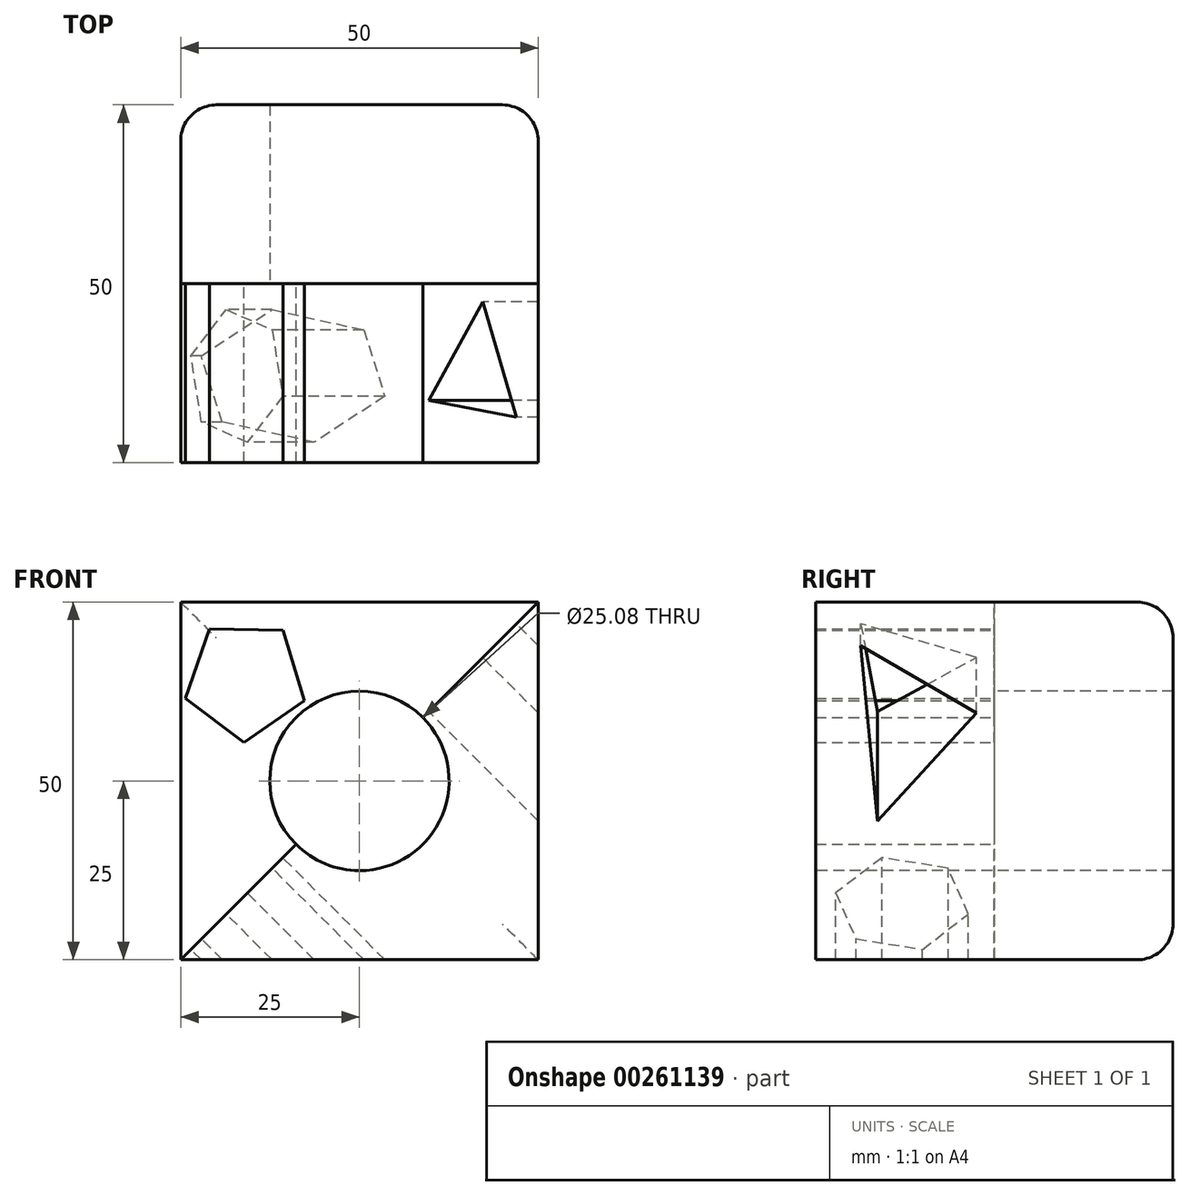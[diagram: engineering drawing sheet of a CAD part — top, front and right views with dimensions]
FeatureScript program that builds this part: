
annotation { "Feature Type Name" : "Feature", "Feature Type Description" : "" }
export const myFeature = defineFeature(function(context is Context, id is Id, definition is map)
    precondition{}
    {
        {
            var Q0;
            Q0=qCreatedBy(makeId("Front.planeOp"),FACE);
            var sketch = newSketch(context, id + "F0", { "sketchPlane" : qUnion([Q0])});
            skLineSegment(sketch, "E0", {"start": v(-25, 25) * mm, "end": v(-25, -25) * mm});
            skLineSegment(sketch, "E1", {"start": v(-25, -25) * mm, "end": v(25, -25) * mm});
            skLineSegment(sketch, "E2", {"start": v(25, -25) * mm, "end": v(25, 25) * mm});
            skLineSegment(sketch, "E3", {"start": v(25, 25) * mm, "end": v(-25, 25) * mm});
            skSolve(sketch);
        }
        {
            var Q0;
            Q0=makeQuery(id+"F0.imprint","IMPRINT",FACE,{"disambiguationData":[TD([[makeQuery(id+"F0.imprint","IMPRINT",EDGE,{"derivedFrom":sQuery(id+"F0.wireOp",EDGE,"E0")}),1.0]])]});
            extrude(context, id + "F1", {"entities" : qUnion([Q0]), "depth" : 25 * mm});
        }
        {
            var Q0;
            Q0=makeQuery(id+"F1.opExtrude","CAP_FACE",FACE,{"disambiguationData":[OSD([sQuery(id+"F0.wireOp",EDGE,"E0"),sQuery(id+"F0.wireOp",EDGE,"E1"),sQuery(id+"F0.wireOp",EDGE,"E2"),sQuery(id+"F0.wireOp",EDGE,"E3")])],"isStart":false});
            var sketch = newSketch(context, id + "F2", { "sketchPlane" : qUnion([Q0])});
            skCircle(sketch, "E4", {"center": v(0, 0) * mm, "radius": 12.54 * mm});
            skSolve(sketch);
        }
        {
            var Q0;
            Q0=makeQuery(id+"F2.imprint","IMPRINT",FACE,{"disambiguationData":[TD([[makeQuery(id+"F2.imprint","IMPRINT",EDGE,{"derivedFrom":sQuery(id+"F2.wireOp",EDGE,"E4")}),1.0]])]});
            extrude(context, id + "F3", {"entities" : qUnion([Q0]), "operationType" : NewBodyOperationType.REMOVE, "oppositeDirection" : true, "depth" : 25 * mm});
        }
        {
            var Q0;
            Q0=makeQuery(id+"F1.opExtrude","CAP_FACE",FACE,{"disambiguationData":[OSD([sQuery(id+"F0.wireOp",EDGE,"E0"),sQuery(id+"F0.wireOp",EDGE,"E1"),sQuery(id+"F0.wireOp",EDGE,"E2"),sQuery(id+"F0.wireOp",EDGE,"E3")])],"isStart":false});
            var sketch = newSketch(context, id + "F4", { "sketchPlane" : qUnion([Q0])});
            skLineSegment(sketch, "E5", {"start": v(-25, -25) * mm, "end": v(-8.84, -8.84) * mm});
            skLineSegment(sketch, "E6", {"start": v(25, 25) * mm, "end": v(25, -25) * mm});
            skLineSegment(sketch, "E7", {"start": v(25, -25) * mm, "end": v(-25, -25) * mm});
            skCircle(sketch, "E8", {"center": v(0, 0) * mm, "radius": 12.5 * mm});
            skLineSegment(sketch, "E9.trimOffspring", {"start": v(8.84, 8.84) * mm, "end": v(25, 25) * mm});
            skSolve(sketch);
        }
        {
            var Q0;
            {var subQ1=sQuery(id+"F4.wireOp",EDGE,"E6");Q0=makeQuery(id+"F4.imprint","IMPRINT",FACE,{"disambiguationData":[TD([[makeQuery(id+"F4.imprint","IMPRINT",EDGE,{"derivedFrom":subQ1}),1.0]])]});}
            extrude(context, id + "F5", {"entities" : qUnion([Q0]), "operationType" : NewBodyOperationType.ADD, "depth" : 25 * mm});
        }
        {
            var Q0;
            Q0=makeQuery(id+"F5.opExtrude","SWEPT_FACE",FACE,{"disambiguationData":[OSD([sQuery(id+"F4.wireOp",EDGE,"E5")])]});
            var sketch = newSketch(context, id + "F6", { "sketchPlane" : qUnion([Q0])});
            skCircle(sketch, "E10.cCircle", {"center": v(37.9, -24.24) * mm, "radius": 8.23 * mm, "construction": true});
            skLineSegment(sketch, "E10.0", {"start": v(35.06, -33.31) * mm, "end": v(28.62, -26.33) * mm});
            skLineSegment(sketch, "E10.1", {"start": v(28.62, -26.33) * mm, "end": v(31.46, -17.25) * mm});
            skLineSegment(sketch, "E10.2", {"start": v(31.46, -17.25) * mm, "end": v(40.73, -15.17) * mm});
            skLineSegment(sketch, "E10.3", {"start": v(40.73, -15.17) * mm, "end": v(47.17, -22.16) * mm});
            skLineSegment(sketch, "E10.4", {"start": v(47.17, -22.16) * mm, "end": v(44.33, -31.23) * mm});
            skLineSegment(sketch, "E10.5", {"start": v(44.33, -31.23) * mm, "end": v(35.06, -33.31) * mm});
            skPoint(sketch, "E10.0.midPoint", {"position": v(31.84, -29.82) * mm});
            skCircle(sketch, "E11.cCircle", {"center": v(37.5, 23.05) * mm, "radius": 5.05 * mm, "construction": true});
            skPoint(sketch, "E11.cCircle.centerSnap0", {"position": v(37.5, -12.54) * mm});
            skLineSegment(sketch, "E11.0", {"start": v(41.34, 13.71) * mm, "end": v(27.5, 24.4) * mm});
            skLineSegment(sketch, "E11.1", {"start": v(27.5, 24.4) * mm, "end": v(43.66, 31.04) * mm});
            skLineSegment(sketch, "E11.2", {"start": v(43.66, 31.04) * mm, "end": v(41.34, 13.71) * mm});
            skPoint(sketch, "E11.0.midPoint", {"position": v(34.42, 19.05) * mm});
            skSolve(sketch);
        }
        {
            var Q0;
            Q0=makeQuery(id+"F6.imprint","IMPRINT",FACE,{"disambiguationData":[TD([[makeQuery(id+"F6.imprint","IMPRINT",EDGE,{"derivedFrom":sQuery(id+"F6.wireOp",EDGE,"E10.0")}),-1.0]])]});
            var Q1;
            Q1=makeQuery(id+"F6.imprint","IMPRINT",FACE,{"disambiguationData":[TD([[makeQuery(id+"F6.imprint","IMPRINT",EDGE,{"derivedFrom":sQuery(id+"F6.wireOp",EDGE,"E11.0")}),-1.0]])]});
            extrude(context, id + "F7", {"entities" : qUnion([Q0, Q1]), "operationType" : NewBodyOperationType.REMOVE, "oppositeDirection" : true, "depth" : 50 * mm});
        }
        {
            var Q0;
            Q0=makeQuery(id+"F1.opExtrude","CAP_FACE",FACE,{"disambiguationData":[OSD([sQuery(id+"F0.wireOp",EDGE,"E0"),sQuery(id+"F0.wireOp",EDGE,"E1"),sQuery(id+"F0.wireOp",EDGE,"E2"),sQuery(id+"F0.wireOp",EDGE,"E3")])],"isStart":false});
            var sketch = newSketch(context, id + "F8", { "sketchPlane" : qUnion([Q0])});
            skCircle(sketch, "E12.cCircle", {"center": v(-15.97, 14.1) * mm, "radius": 7.08 * mm, "construction": true});
            skLineSegment(sketch, "E12.0", {"start": v(-24.34, 11.55) * mm, "end": v(-20.98, 21.28) * mm});
            skLineSegment(sketch, "E12.1", {"start": v(-20.98, 21.28) * mm, "end": v(-10.69, 21.08) * mm});
            skLineSegment(sketch, "E12.2", {"start": v(-10.69, 21.08) * mm, "end": v(-7.7, 11.24) * mm});
            skLineSegment(sketch, "E12.3", {"start": v(-7.7, 11.24) * mm, "end": v(-16.13, 5.35) * mm});
            skLineSegment(sketch, "E12.4", {"start": v(-16.13, 5.35) * mm, "end": v(-24.34, 11.55) * mm});
            skPoint(sketch, "E12.0.midPoint", {"position": v(-22.66, 16.42) * mm});
            skSolve(sketch);
        }
        {
            var Q0;
            Q0=makeQuery(id+"F8.imprint","IMPRINT",FACE,{"disambiguationData":[TD([[makeQuery(id+"F8.imprint","IMPRINT",EDGE,{"derivedFrom":sQuery(id+"F8.wireOp",EDGE,"E12.0")}),-1.0]])]});
            extrude(context, id + "F9", {"entities" : qUnion([Q0]), "operationType" : NewBodyOperationType.ADD, "depth" : 25 * mm});
        }
        {
            var Q0;
            Q0=makeQuery(id+"F1.opExtrude","CAP_EDGE",EDGE,{"disambiguationData":[OSD([sQuery(id+"F0.wireOp",EDGE,"E2")])],"isStart":true});
            var Q1;
            Q1=makeQuery(id+"F1.opExtrude","CAP_EDGE",EDGE,{"disambiguationData":[OSD([sQuery(id+"F0.wireOp",EDGE,"E3")])],"isStart":true});
            var Q2;
            Q2=makeQuery(id+"F1.opExtrude","CAP_EDGE",EDGE,{"disambiguationData":[OSD([sQuery(id+"F0.wireOp",EDGE,"E0")])],"isStart":true});
            var Q3;
            Q3=makeQuery(id+"F1.opExtrude","CAP_EDGE",EDGE,{"disambiguationData":[OSD([sQuery(id+"F0.wireOp",EDGE,"E1")])],"isStart":true});
            fillet(context, id + "F10", {"entities" : qUnion([Q0, Q1, Q2, Q3]), "radius" : 5 * mm, "tangentPropagation" : true, "allowEdgeOverflow" : false});
        }
    });
